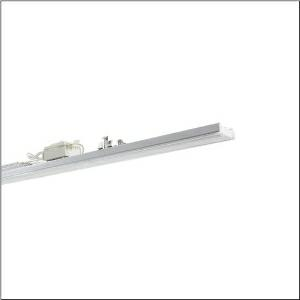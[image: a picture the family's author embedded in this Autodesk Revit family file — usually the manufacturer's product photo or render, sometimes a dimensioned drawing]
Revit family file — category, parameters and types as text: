
# Revit family: licross_r__11_recessed_ho_51te11dv4m2s_7c13
name_source: partatom
category: Lighting Fixtures
units: mm (PartAtom-declared; Revit-internal decimal feet)

## family parameters
Cut with Voids When Loaded = No
Host = Face
Light Source = No
Part Type = Normal
Room Calculation Point = No
Round Connector Dimension = Use Diameter
Shared = No

## types (1)
- --- (1 x LED, 27080 lm, 150.5 W, 4000K)
    Apparent Load = 150 VA
    CIE Flux Codes = 87 95 99 100 100
    Color Rendering = 80
    Color Temperature = 4000K
    Default Elevation = 1800 mm
    Description = Licross® 11 Recessed HO, luminaire insert, of sheet steel, galvanised, coil coated, white, length: 2.250mm, width: 66mm, height: 67mm, LED rated luminous flux: 27.080lm, light colour: 840, control gear: DALI 2, with plug, 5-pole, with phase selection, mains connection: 220..240V, AC, 50/60Hz, rated input power: 151W, internal wiring halogen-free, primary light control with lens, of plastic, primary optical cover: cover, of PMMA, light emission: direct distribution, primary light characteristic: symmetric, protection rating (complete): IP54, insulation class (complete): insulation class I (protective earthing), certification: CE, ENEC, VDE, UKCA, protection symbol: D if used in an environment with non-conductive dust loads with corresponding accessories, impact resistance: IK06, permissible ambient temperature for indoor applications: -40..+35°C, corresponds to IFS (International Featured Standards) requirements for safety and quality in the food industry, reducing of maximum allowable ambient temperature of 5°C with ceiling mounting, LABS conformity tested according to VDMA 24364:2018-05, packaging unit: 1 piece
    Height = 58 mm
    Lamp = 1 x LED
    Lamp Light Flux = 27080 lm
    Lamp Power = 150.5 W
    Lamp count = 1
    Length = 2250 mm
    Luminous efficacy = 180 lm/W
    Manufacturer = Siteco
    ModVariant = No
    Model = 51TE11DV4M2S
    Mounting Place = Ceiling
    Mounting Type = Pendant
    Number of Poles = 1
    OnlyDefault = Yes
    Power Factor = 1
    Product Name = Licross® 11 Recessed HO
    Product group = luminaire insert | ceiling pendant
    ProductGroupID = 902
    Protection Class = Protection class I
    Protection Degree = IP 54
    RLX_Detail_Level = 1
    RLX_Emergency_Light_Flux = 0 lm
    RLX_Emergency_Type = 0
    RLX_Emergency_Type_DB = No
    RlxData = <blob elided: 29709 chars, md5=e84fa32d>
    Socket = socket
    Standby Power = 0 W
    System Light Flux = 27079 lm
    System Power = 150 W
    Type Comments = factory setting: luminous flux: 100 % | dim-lin: 254 | 690 mA
    Type Image = l_1296930.jpg
    URL = http://relux.com
    VarID = @adj_120211
    Voltage = 0 V
    Weight = 0.00 kg
    Width = 66 mm

## geometry (parser evidence)
native form markers: Blend x4, Sweep x10
no freeform markers — native parametric forms only
